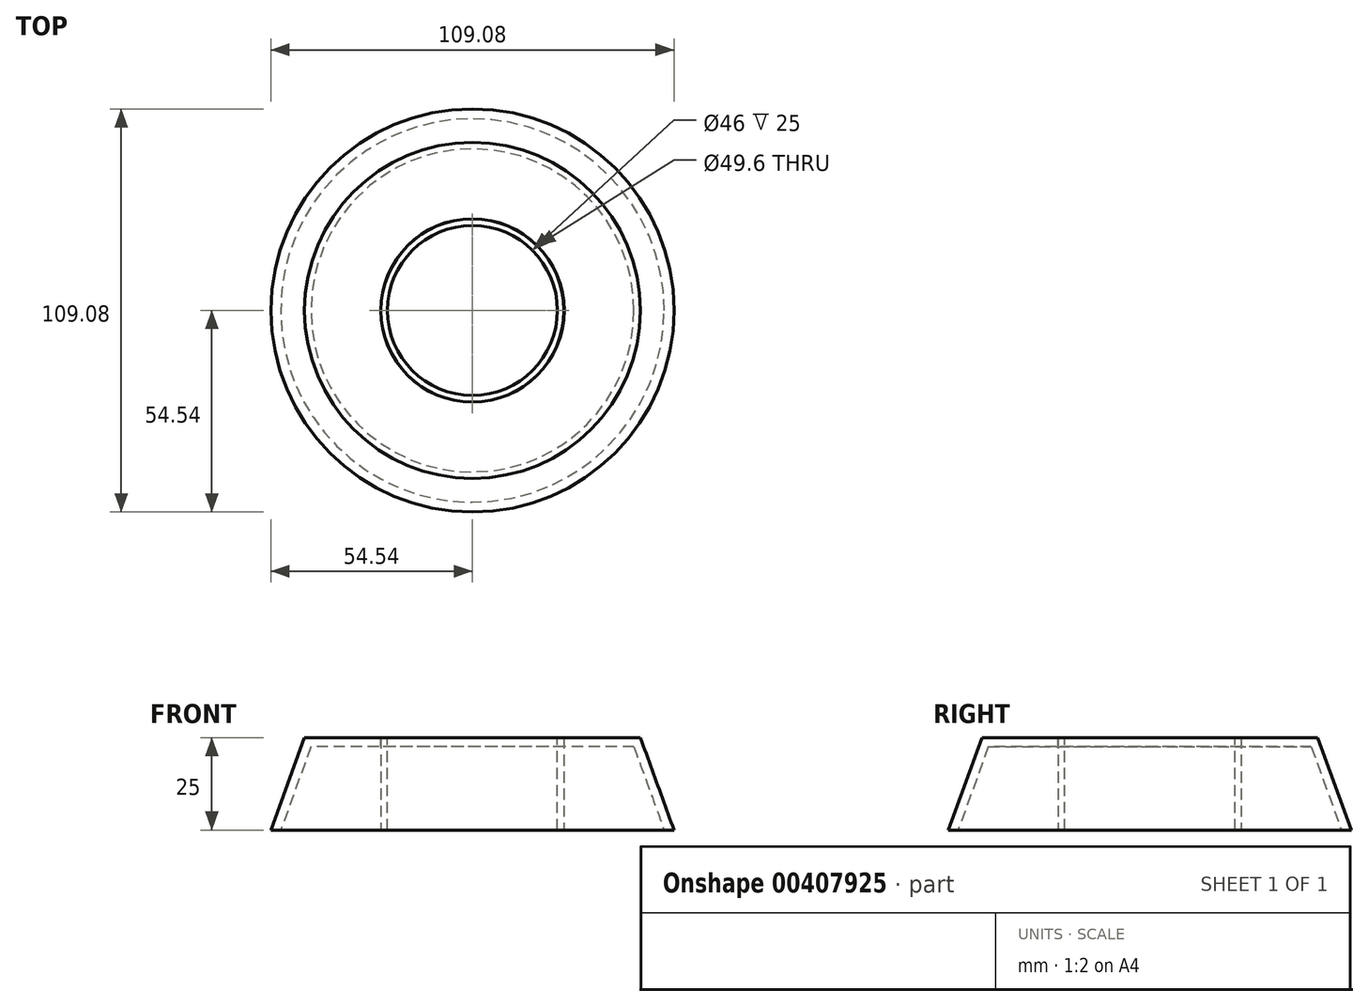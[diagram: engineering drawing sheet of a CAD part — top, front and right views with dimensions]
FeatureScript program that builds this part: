
annotation { "Feature Type Name" : "Feature", "Feature Type Description" : "" }
export const myFeature = defineFeature(function(context is Context, id is Id, definition is map)
    precondition{}
    {
        {
            var Q0;
            Q0=qCreatedBy(makeId("Top.planeOp"),FACE);
            var sketch = newSketch(context, id + "F0", { "sketchPlane" : qUnion([Q0])});
            skCircle(sketch, "E0", {"center": v(0, 0) * mm, "radius": 60 * mm});
            skSolve(sketch);
        }
        {
            var Q0;
            Q0=makeQuery(id+"F0.imprint","IMPRINT",FACE,{"disambiguationData":[TD([[makeQuery(id+"F0.imprint","IMPRINT",EDGE,{"derivedFrom":sQuery(id+"F0.wireOp",EDGE,"E0")}),1.0]])]});
            extrude(context, id + "F1", {"entities" : qUnion([Q0]), "depth" : 25 * mm});
        }
        {
            var Q0;
            Q0=makeQuery(id+"F1.opExtrude","CAP_EDGE",EDGE,{"disambiguationData":[OSD([sQuery(id+"F0.wireOp",EDGE,"E0")])],"isStart":false});
            chamfer(context, id + "F2", {"entities" : qUnion([Q0]), "chamferType" : ChamferType.OFFSET_ANGLE, "width" : 40 * mm, "oppositeDirection" : false, "angle" : 20 * degree, "tangentPropagation" : true});
        }
        {
            var Q0;
            Q0=makeQuery(id+"F1.opExtrude","CAP_FACE",FACE,{"disambiguationData":[OSD([sQuery(id+"F0.wireOp",EDGE,"E0")])],"isStart":true});
            shell(context, id + "F3", {"entities" : qUnion([Q0]), "thickness" : 2.5 * mm});
        }
        {
            var Q0;
            Q0=sQuery(id+"F0.wireOp",VERTEX,"E0.center");
            var Q1;
            Q1=makeQuery(id+"F1.opExtrude","SWEPT_BODY",BODY,{"disambiguationData":[OSD([sQuery(id+"F0.wireOp",EDGE,"E0")])]});
            hole(context, id + "F4", {"style" : HoleStyle.SIMPLE, "endStyle" : HoleEndStyle.THROUGH, "oppositeDirection" : true, "holeDiameter" : 49.6 * mm, "isTappedThrough" : true, "tappedDepth" : 12 * mm, "tapClearance" : 3, "locations" : qUnion([Q0]), "scope" : qUnion([Q1]), "startStyle" : HoleStartStyle.SKETCH});
        }
        {
            var Q0;
            Q0=qCreatedBy(makeId("Top.planeOp"),FACE);
            var sketch = newSketch(context, id + "F5", { "sketchPlane" : qUnion([Q0])});
            skCircle(sketch, "E1", {"center": v(0, 0) * mm, "radius": 24.75 * mm});
            skPoint(sketch, "E2", {"position": v(8.75, -23.15) * mm});
            skPoint(sketch, "E3", {"position": v(-8.68, 23.18) * mm});
            skLineSegment(sketch, "E4", {"start": v(8.75, -23.15) * mm, "end": v(8.75, -40.26) * mm, "construction": true});
            skLineSegment(sketch, "E5", {"start": v(-8.68, 23.18) * mm, "end": v(-8.68, 30.9) * mm, "construction": true});
            skSolve(sketch);
        }
        {
            var Q0;
            Q0 = qSketchRegion(id + "F5", true);
            extrude(context, id + "F6", {"entities" : qUnion([Q0]), "depth" : 25 * mm});
        }
        {
            var Q0;
            Q0=sQuery(id+"F0.wireOp",VERTEX,"E0.center");
            var Q1;
            Q1=makeQuery(id+"F6.opExtrude","SWEPT_BODY",BODY,{"disambiguationData":[OSD([sQuery(id+"F5.wireOp",EDGE,"E1")])]});
            hole(context, id + "F7", {"style" : HoleStyle.SIMPLE, "endStyle" : HoleEndStyle.THROUGH, "oppositeDirection" : true, "holeDiameter" : 46 * mm, "isTappedThrough" : true, "tappedDepth" : 12 * mm, "tapClearance" : 3, "locations" : qUnion([Q0]), "scope" : qUnion([Q1]), "startStyle" : HoleStartStyle.SKETCH});
        }
    });
